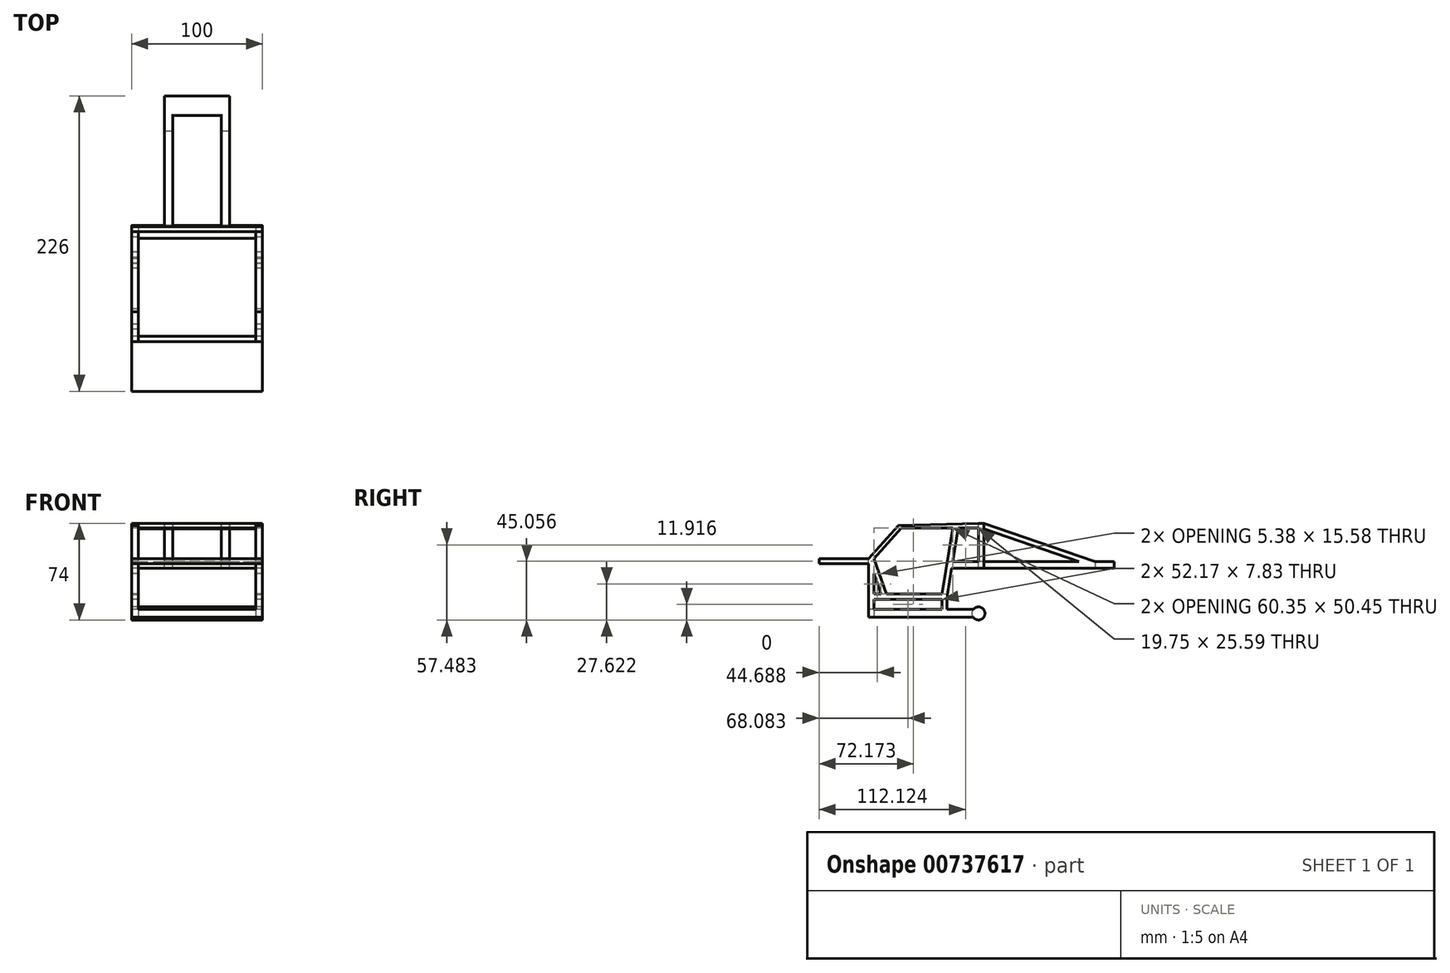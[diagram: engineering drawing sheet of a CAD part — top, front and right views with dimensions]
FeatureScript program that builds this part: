
annotation { "Feature Type Name" : "Feature", "Feature Type Description" : "" }
export const myFeature = defineFeature(function(context is Context, id is Id, definition is map)
    precondition{}
    {
        {
            var Q0;
            Q0=qCreatedBy(makeId("Right.planeOp"),FACE);
            var sketch = newSketch(context, id + "F0", { "sketchPlane" : qUnion([Q0])});
            skLineSegment(sketch, "E0.bottom", {"start": v(35, -26) * mm, "end": v(-45, -26) * mm});
            skLineSegment(sketch, "E0.top", {"start": v(35, -32) * mm, "end": v(-45, -32) * mm});
            skLineSegment(sketch, "E0.left", {"start": v(35, -26) * mm, "end": v(35, -32) * mm});
            skLineSegment(sketch, "E0.right", {"start": v(-45, -26) * mm, "end": v(-45, -32) * mm});
            skLineSegment(sketch, "E1.bottom", {"start": v(35, -32) * mm, "end": v(39, -32) * mm});
            skLineSegment(sketch, "E1.top", {"start": v(35, 40) * mm, "end": v(39, 40) * mm});
            skLineSegment(sketch, "E1.left", {"start": v(35, -32) * mm, "end": v(35, 40) * mm});
            skLineSegment(sketch, "E1.right", {"start": v(39, -32) * mm, "end": v(39, 40) * mm});
            skLineSegment(sketch, "E2", {"start": v(35, -26) * mm, "end": v(39, -26) * mm});
            skLineSegment(sketch, "E3.bottom", {"start": v(-45, -32) * mm, "end": v(-49, -32) * mm});
            skLineSegment(sketch, "E3.top", {"start": v(-45, 13) * mm, "end": v(-49, 13) * mm});
            skLineSegment(sketch, "E3.left", {"start": v(-45, -32) * mm, "end": v(-45, 13) * mm});
            skLineSegment(sketch, "E3.right", {"start": v(-49, -32) * mm, "end": v(-49, 13) * mm});
            skLineSegment(sketch, "E4", {"start": v(-45, -26) * mm, "end": v(-49, -26) * mm});
            skLineSegment(sketch, "E5", {"start": v(-49, 13) * mm, "end": v(-26.27, 38.28) * mm});
            skLineSegment(sketch, "E6", {"start": v(-26.27, 38.28) * mm, "end": v(-24.04, 36.28) * mm});
            skLineSegment(sketch, "E7", {"start": v(-24.04, 36.28) * mm, "end": v(-45, 13) * mm});
            skLineSegment(sketch, "E8", {"start": v(35, 40) * mm, "end": v(-26.27, 38.28) * mm});
            skLineSegment(sketch, "E9", {"start": v(-24.04, 36.28) * mm, "end": v(35, 36.28) * mm});
            skLineSegment(sketch, "E10", {"start": v(-45, 13) * mm, "end": v(-35.62, -14.17) * mm});
            skLineSegment(sketch, "E11", {"start": v(-35.62, -14.17) * mm, "end": v(7.17, -14.17) * mm});
            skLineSegment(sketch, "E12", {"start": v(7.17, -14.17) * mm, "end": v(15.86, 39.46) * mm});
            skLineSegment(sketch, "E13", {"start": v(7.17, -14.17) * mm, "end": v(11.11, -14.8) * mm});
            skLineSegment(sketch, "E14", {"start": v(11.11, -14.8) * mm, "end": v(19.91, 39.46) * mm});
            skLineSegment(sketch, "E15", {"start": v(-49, 13) * mm, "end": v(-39.62, -14.17) * mm});
            skLineSegment(sketch, "E16", {"start": v(-39.62, -14.17) * mm, "end": v(-35.62, -14.17) * mm});
            skLineSegment(sketch, "E17", {"start": v(-39.62, -14.17) * mm, "end": v(-39.62, -18.17) * mm});
            skLineSegment(sketch, "E18", {"start": v(-39.62, -18.17) * mm, "end": v(10.75, -18.17) * mm});
            skLineSegment(sketch, "E19", {"start": v(10.75, -18.17) * mm, "end": v(11.11, -14.8) * mm});
            skLineSegment(sketch, "E20", {"start": v(7.17, -14.17) * mm, "end": v(7.17, -18.17) * mm});
            skLineSegment(sketch, "E21", {"start": v(7.17, -18.17) * mm, "end": v(7.17, -26) * mm});
            skLineSegment(sketch, "E22", {"start": v(10.75, -18.17) * mm, "end": v(10.75, -26) * mm});
            skLineSegment(sketch, "E23", {"start": v(10.75, -26) * mm, "end": v(7.17, -26) * mm});
            skLineSegment(sketch, "E24.bottom", {"start": v(-39.62, -18.17) * mm, "end": v(-45, -18.17) * mm});
            skLineSegment(sketch, "E24.top", {"start": v(-39.62, -14.17) * mm, "end": v(-45, -14.17) * mm});
            skLineSegment(sketch, "E24.left", {"start": v(-39.62, -18.17) * mm, "end": v(-39.62, -14.17) * mm});
            skLineSegment(sketch, "E24.right", {"start": v(-45, -18.17) * mm, "end": v(-45, -14.17) * mm});
            skCircle(sketch, "E25", {"center": v(35, -29) * mm, "radius": 5 * mm});
            skLineSegment(sketch, "E26.bottom", {"start": v(39, 10.69) * mm, "end": v(111.81, 10.69) * mm});
            skLineSegment(sketch, "E26.top", {"start": v(39, 5.69) * mm, "end": v(139, 5.69) * mm});
            skLineSegment(sketch, "E26.left", {"start": v(39, 10.69) * mm, "end": v(39, 5.69) * mm});
            skLineSegment(sketch, "E26.right", {"start": v(139, 10.69) * mm, "end": v(139, 5.69) * mm});
            skLineSegment(sketch, "E27.bottom", {"start": v(39, 5.69) * mm, "end": v(14.44, 5.69) * mm});
            skLineSegment(sketch, "E27.top", {"start": v(39, 10.69) * mm, "end": v(15.25, 10.69) * mm});
            skLineSegment(sketch, "E27.left", {"start": v(39, 5.69) * mm, "end": v(39, 10.69) * mm});
            skPoint(sketch, "E27.right.end.orphan", {"position": v(11.2, 10.69) * mm});
            skLineSegment(sketch, "E28", {"start": v(39, 40) * mm, "end": v(124.1, 10.69) * mm});
            skLineSegment(sketch, "E29", {"start": v(111.81, 10.69) * mm, "end": v(39, 35.77) * mm});
            skPoint(sketch, "E29.endSnap0", {"position": v(37, 40) * mm});
            skLineSegment(sketch, "E30.trimOffspring", {"start": v(124.1, 10.69) * mm, "end": v(139, 10.69) * mm});
            skLineSegment(sketch, "E31", {"start": v(-49, 13) * mm, "end": v(-87, 13) * mm});
            skLineSegment(sketch, "E32", {"start": v(-87, 13) * mm, "end": v(-87, 9) * mm});
            skLineSegment(sketch, "E33", {"start": v(-87, 9) * mm, "end": v(-49, 9) * mm});
            skLineSegment(sketch, "E34", {"start": v(10.75, -26) * mm, "end": v(10.75, -32) * mm});
            skLineSegment(sketch, "E35", {"start": v(39, 35.77) * mm, "end": v(35, 36.28) * mm});
            skSolve(sketch);
        }
        {
            var Q0;
            {var subQ0=sQuery(id+"F0.wireOp",EDGE,"E4");Q0=makeQuery(id+"F0.imprint","IMPRINT",FACE,{"disambiguationData":[TD([[makeQuery(id+"F0.imprint","IMPRINT",EDGE,{"derivedFrom":subQ0}),-1.0]])]});}
            var Q1;
            Q1=makeQuery(id+"F0.imprint","IMPRINT",FACE,{"disambiguationData":[TD([[makeQuery(id+"F0.imprint","IMPRINT",EDGE,{"derivedFrom":sQuery(id+"F0.wireOp",EDGE,"E0.right")}),-1.0]])]});
            var Q2;
            Q2=makeQuery(id+"F0.imprint","IMPRINT",FACE,{"disambiguationData":[TD([[makeQuery(id+"F0.imprint","IMPRINT",EDGE,{"derivedFrom":sQuery(id+"F0.wireOp",EDGE,"E3.top")}),-1.0]])]});
            var Q3;
            {var subQ0=sQuery(id+"F0.wireOp",EDGE,"E6");Q3=makeQuery(id+"F0.imprint","IMPRINT",FACE,{"disambiguationData":[TD([[makeQuery(id+"F0.imprint","IMPRINT",EDGE,{"derivedFrom":subQ0}),1.0]])]});}
            var Q4;
            {var subQ0=sQuery(id+"F0.wireOp",EDGE,"E9");var subQ1=makeQuery(id+"F0.imprint","INTERSECT",VERTEX,{"derivedFrom":[subQ0,sQuery(id+"F0.wireOp",EDGE,"E14")]});Q4=makeQuery(id+"F0.imprint","IMPRINT",FACE,{"disambiguationData":[TD([[makeQuery(id+"F0.imprint","IMPRINT",EDGE,{"disambiguationData":[TD([[subQ1,1.0]])],"derivedFrom":subQ0}),1.0]])]});}
            var Q5;
            {var subQ0=sQuery(id+"F0.wireOp",EDGE,"E3.top");Q5=makeQuery(id+"F0.imprint","IMPRINT",FACE,{"disambiguationData":[TD([[makeQuery(id+"F0.imprint","IMPRINT",EDGE,{"derivedFrom":subQ0}),1.0]])]});}
            var Q6;
            {var subQ0=sQuery(id+"F0.wireOp",EDGE,"E10");Q6=makeQuery(id+"F0.imprint","IMPRINT",FACE,{"disambiguationData":[TD([[makeQuery(id+"F0.imprint","IMPRINT",EDGE,{"derivedFrom":subQ0}),-1.0]])]});}
            var Q7;
            Q7=makeQuery(id+"F0.imprint","IMPRINT",FACE,{"disambiguationData":[TD([[makeQuery(id+"F0.imprint","IMPRINT",EDGE,{"derivedFrom":sQuery(id+"F0.wireOp",EDGE,"E11")}),-1.0]])]});
            var Q8;
            Q8=makeQuery(id+"F0.imprint","IMPRINT",FACE,{"disambiguationData":[TD([[makeQuery(id+"F0.imprint","IMPRINT",EDGE,{"derivedFrom":sQuery(id+"F0.wireOp",EDGE,"E13")}),-1.0]])]});
            var Q9;
            {var subQ4=sQuery(id+"F0.wireOp",EDGE,"E13");Q9=makeQuery(id+"F0.imprint","IMPRINT",FACE,{"disambiguationData":[TD([[makeQuery(id+"F0.imprint","IMPRINT",EDGE,{"derivedFrom":subQ4}),1.0]])]});}
            var Q10;
            {var subQ4=sQuery(id+"F0.wireOp",EDGE,"E13");Q10=makeQuery(id+"F0.imprint","IMPRINT",FACE,{"disambiguationData":[TD([[makeQuery(id+"F0.imprint","IMPRINT",EDGE,{"derivedFrom":subQ4}),1.0]])]});}
            var Q11;
            Q11=makeQuery(id+"F0.imprint","IMPRINT",FACE,{"disambiguationData":[TD([[makeQuery(id+"F0.imprint","IMPRINT",EDGE,{"derivedFrom":sQuery(id+"F0.wireOp",EDGE,"E17")}),-1.0]])]});
            var Q12;
            {var subQ0=sQuery(id+"F0.wireOp",EDGE,"E21");Q12=makeQuery(id+"F0.imprint","IMPRINT",FACE,{"disambiguationData":[TD([[makeQuery(id+"F0.imprint","IMPRINT",EDGE,{"derivedFrom":subQ0}),1.0]])]});}
            var Q13;
            {var subQ2=sQuery(id+"F0.wireOp",EDGE,"E0.right");Q13=makeQuery(id+"F0.imprint","IMPRINT",FACE,{"disambiguationData":[TD([[makeQuery(id+"F0.imprint","IMPRINT",EDGE,{"derivedFrom":subQ2}),1.0]])]});}
            var Q14;
            {var subQ0=sQuery(id+"F0.wireOp",EDGE,"E1.left");var subQ3=sQuery(id+"F0.wireOp",EDGE,"E25");var subQ5=makeQuery(id+"F0.imprint","INTERSECT",VERTEX,{"derivedFrom":[subQ0,subQ3]});Q14=makeQuery(id+"F0.imprint","IMPRINT",FACE,{"disambiguationData":[TD([[makeQuery(id+"F0.imprint","IMPRINT",EDGE,{"disambiguationData":[TD([[subQ5,-1.0]])],"derivedFrom":subQ3}),1.0]])]});}
            var Q15;
            {var subQ0=sQuery(id+"F0.wireOp",EDGE,"E0.left");Q15=makeQuery(id+"F0.imprint","IMPRINT",FACE,{"disambiguationData":[TD([[makeQuery(id+"F0.imprint","IMPRINT",EDGE,{"derivedFrom":subQ0}),-1.0]])]});}
            var Q16;
            {var subQ3=sQuery(id+"F0.wireOp",EDGE,"E1.bottom");Q16=makeQuery(id+"F0.imprint","IMPRINT",FACE,{"disambiguationData":[TD([[makeQuery(id+"F0.imprint","IMPRINT",EDGE,{"derivedFrom":subQ3}),-1.0]])]});}
            var Q17;
            Q17=makeQuery(id+"F0.imprint","IMPRINT",FACE,{"disambiguationData":[TD([[makeQuery(id+"F0.imprint","IMPRINT",EDGE,{"derivedFrom":sQuery(id+"F0.wireOp",EDGE,"E0.left")}),1.0]])]});
            var Q18;
            {var subQ0=sQuery(id+"F0.wireOp",EDGE,"E2");Q18=makeQuery(id+"F0.imprint","IMPRINT",FACE,{"disambiguationData":[TD([[makeQuery(id+"F0.imprint","IMPRINT",EDGE,{"derivedFrom":subQ0}),1.0]])]});}
            var Q19;
            {var subQ0=sQuery(id+"F0.wireOp",EDGE,"E25");var subQ1=sQuery(id+"F0.wireOp",EDGE,"E1.right");var subQ2=makeQuery(id+"F0.imprint","INTERSECT",VERTEX,{"derivedFrom":[sQuery(id+"F0.wireOp",EDGE,"E1.bottom"),subQ1,subQ0]});Q19=makeQuery(id+"F0.imprint","IMPRINT",FACE,{"disambiguationData":[TD([[makeQuery(id+"F0.imprint","IMPRINT",EDGE,{"disambiguationData":[TD([[subQ2,-1.0]])],"derivedFrom":subQ1}),-1.0]])]});}
            var Q20;
            {var subQ0=sQuery(id+"F0.wireOp",EDGE,"E34");Q20=makeQuery(id+"F0.imprint","IMPRINT",FACE,{"disambiguationData":[TD([[makeQuery(id+"F0.imprint","IMPRINT",EDGE,{"derivedFrom":subQ0}),1.0]])]});}
            var Q21;
            {var subQ0=sQuery(id+"F0.wireOp",EDGE,"E27.bottom");var subQ1=sQuery(id+"F0.wireOp",EDGE,"E1.left");var subQ2=makeQuery(id+"F0.imprint","INTERSECT",VERTEX,{"derivedFrom":[subQ1,subQ0]});Q21=makeQuery(id+"F0.imprint","IMPRINT",FACE,{"disambiguationData":[TD([[makeQuery(id+"F0.imprint","IMPRINT",EDGE,{"disambiguationData":[TD([[subQ2,-1.0]])],"derivedFrom":subQ1}),1.0]])]});}
            var Q22;
            {var subQ0=sQuery(id+"F0.wireOp",EDGE,"E1.top");Q22=makeQuery(id+"F0.imprint","IMPRINT",FACE,{"disambiguationData":[TD([[makeQuery(id+"F0.imprint","IMPRINT",EDGE,{"derivedFrom":subQ0}),-1.0]])]});}
            var Q23;
            {var subQ0=sQuery(id+"F0.wireOp",EDGE,"E27.bottom");var subQ1=sQuery(id+"F0.wireOp",EDGE,"E1.left");var subQ2=makeQuery(id+"F0.imprint","INTERSECT",VERTEX,{"derivedFrom":[subQ1,subQ0]});Q23=makeQuery(id+"F0.imprint","IMPRINT",FACE,{"disambiguationData":[TD([[makeQuery(id+"F0.imprint","IMPRINT",EDGE,{"disambiguationData":[TD([[subQ2,-1.0]])],"derivedFrom":subQ1}),-1.0]])]});}
            var Q24;
            {var subQ0=sQuery(id+"F0.wireOp",EDGE,"E31");Q24=makeQuery(id+"F0.imprint","IMPRINT",FACE,{"disambiguationData":[TD([[makeQuery(id+"F0.imprint","IMPRINT",EDGE,{"derivedFrom":subQ0}),1.0]])]});}
            var Q25;
            {var subQ3=sQuery(id+"F0.wireOp",EDGE,"E35");Q25=makeQuery(id+"F0.imprint","IMPRINT",FACE,{"disambiguationData":[TD([[makeQuery(id+"F0.imprint","IMPRINT",EDGE,{"derivedFrom":subQ3}),1.0]])]});}
            extrude(context, id + "F1", {"entities" : qUnion([Q0, Q1, Q2, Q3, Q4, Q5, Q6, Q7, Q8, Q9, Q10, Q11, Q12, Q13, Q14, Q15, Q16, Q17, Q18, Q19, Q20, Q21, Q22, Q23, Q24, Q25]), "endBound" : BoundingType.SYMMETRIC, "depth" : 100 * mm, "offsetDistance" : 25 * mm});
        }
        {
            var Q0;
            {var subQ3=sQuery(id+"F0.wireOp",EDGE,"E35");Q0=makeQuery(id+"F0.imprint","IMPRINT",FACE,{"disambiguationData":[TD([[makeQuery(id+"F0.imprint","IMPRINT",EDGE,{"derivedFrom":subQ3}),1.0]])]});}
            extrude(context, id + "F2", {"entities" : qUnion([Q0]), "operationType" : NewBodyOperationType.REMOVE, "endBound" : BoundingType.SYMMETRIC, "oppositeDirection" : true, "depth" : 90 * mm, "offsetDistance" : 25 * mm});
        }
        {
            var Q0;
            {var subQ4=sQuery(id+"F0.wireOp",EDGE,"E13");Q0=makeQuery(id+"F0.imprint","IMPRINT",FACE,{"disambiguationData":[TD([[makeQuery(id+"F0.imprint","IMPRINT",EDGE,{"derivedFrom":subQ4}),1.0]])]});}
            var Q1;
            {var subQ0=sQuery(id+"F0.wireOp",EDGE,"E6");Q1=makeQuery(id+"F0.imprint","IMPRINT",FACE,{"disambiguationData":[TD([[makeQuery(id+"F0.imprint","IMPRINT",EDGE,{"derivedFrom":subQ0}),1.0]])]});}
            var Q2;
            {var subQ0=sQuery(id+"F0.wireOp",EDGE,"E9");var subQ1=makeQuery(id+"F0.imprint","INTERSECT",VERTEX,{"derivedFrom":[subQ0,sQuery(id+"F0.wireOp",EDGE,"E14")]});Q2=makeQuery(id+"F0.imprint","IMPRINT",FACE,{"disambiguationData":[TD([[makeQuery(id+"F0.imprint","IMPRINT",EDGE,{"disambiguationData":[TD([[subQ1,1.0]])],"derivedFrom":subQ0}),1.0]])]});}
            var Q3;
            Q3=makeQuery(id+"F0.imprint","IMPRINT",FACE,{"disambiguationData":[TD([[makeQuery(id+"F0.imprint","IMPRINT",EDGE,{"derivedFrom":sQuery(id+"F0.wireOp",EDGE,"E3.top")}),-1.0]])]});
            var Q4;
            {var subQ0=sQuery(id+"F0.wireOp",EDGE,"E3.top");Q4=makeQuery(id+"F0.imprint","IMPRINT",FACE,{"disambiguationData":[TD([[makeQuery(id+"F0.imprint","IMPRINT",EDGE,{"derivedFrom":subQ0}),1.0]])]});}
            var Q5;
            {var subQ0=sQuery(id+"F0.wireOp",EDGE,"E10");Q5=makeQuery(id+"F0.imprint","IMPRINT",FACE,{"disambiguationData":[TD([[makeQuery(id+"F0.imprint","IMPRINT",EDGE,{"derivedFrom":subQ0}),-1.0]])]});}
            var Q6;
            Q6=makeQuery(id+"F0.imprint","IMPRINT",FACE,{"disambiguationData":[TD([[makeQuery(id+"F0.imprint","IMPRINT",EDGE,{"derivedFrom":sQuery(id+"F0.wireOp",EDGE,"E11")}),-1.0]])]});
            var Q7;
            Q7=makeQuery(id+"F0.imprint","IMPRINT",FACE,{"disambiguationData":[TD([[makeQuery(id+"F0.imprint","IMPRINT",EDGE,{"derivedFrom":sQuery(id+"F0.wireOp",EDGE,"E13")}),-1.0]])]});
            var Q8;
            Q8=makeQuery(id+"F0.imprint","IMPRINT",FACE,{"disambiguationData":[TD([[makeQuery(id+"F0.imprint","IMPRINT",EDGE,{"derivedFrom":sQuery(id+"F0.wireOp",EDGE,"E17")}),-1.0]])]});
            var Q9;
            {var subQ0=sQuery(id+"F0.wireOp",EDGE,"E21");Q9=makeQuery(id+"F0.imprint","IMPRINT",FACE,{"disambiguationData":[TD([[makeQuery(id+"F0.imprint","IMPRINT",EDGE,{"derivedFrom":subQ0}),1.0]])]});}
            var Q10;
            {var subQ2=sQuery(id+"F0.wireOp",EDGE,"E0.right");Q10=makeQuery(id+"F0.imprint","IMPRINT",FACE,{"disambiguationData":[TD([[makeQuery(id+"F0.imprint","IMPRINT",EDGE,{"derivedFrom":subQ2}),1.0]])]});}
            var Q11;
            {var subQ0=sQuery(id+"F0.wireOp",EDGE,"E34");Q11=makeQuery(id+"F0.imprint","IMPRINT",FACE,{"disambiguationData":[TD([[makeQuery(id+"F0.imprint","IMPRINT",EDGE,{"derivedFrom":subQ0}),1.0]])]});}
            var Q12;
            {var subQ0=sQuery(id+"F0.wireOp",EDGE,"E27.bottom");var subQ1=sQuery(id+"F0.wireOp",EDGE,"E1.left");var subQ2=makeQuery(id+"F0.imprint","INTERSECT",VERTEX,{"derivedFrom":[subQ1,subQ0]});Q12=makeQuery(id+"F0.imprint","IMPRINT",FACE,{"disambiguationData":[TD([[makeQuery(id+"F0.imprint","IMPRINT",EDGE,{"disambiguationData":[TD([[subQ2,-1.0]])],"derivedFrom":subQ1}),1.0]])]});}
            extrude(context, id + "F3", {"entities" : qUnion([Q0, Q1, Q2, Q3, Q4, Q5, Q6, Q7, Q8, Q9, Q10, Q11, Q12]), "operationType" : NewBodyOperationType.REMOVE, "endBound" : BoundingType.SYMMETRIC, "oppositeDirection" : true, "depth" : 90 * mm, "offsetDistance" : 25 * mm});
        }
        {
            var Q0;
            {var subQ0=sQuery(id+"F0.wireOp",EDGE,"E4");Q0=makeQuery(id+"F0.imprint","IMPRINT",FACE,{"disambiguationData":[TD([[makeQuery(id+"F0.imprint","IMPRINT",EDGE,{"derivedFrom":subQ0}),-1.0]])]});}
            extrude(context, id + "F4", {"entities" : qUnion([Q0]), "operationType" : NewBodyOperationType.REMOVE, "endBound" : BoundingType.SYMMETRIC, "oppositeDirection" : true, "depth" : 90 * mm, "offsetDistance" : 25 * mm});
        }
        {
            var Q0;
            {var subQ1=sQuery(id+"F0.wireOp",EDGE,"E26.bottom");Q0=makeQuery(id+"F0.imprint","IMPRINT",FACE,{"disambiguationData":[TD([[makeQuery(id+"F0.imprint","IMPRINT",EDGE,{"derivedFrom":subQ1}),-1.0]])]});}
            extrude(context, id + "F5", {"entities" : qUnion([Q0]), "operationType" : NewBodyOperationType.ADD, "endBound" : BoundingType.SYMMETRIC, "depth" : 50 * mm, "offsetDistance" : 25 * mm});
        }
        {
            var Q0;
            {var subQ1=sQuery(id+"F0.wireOp",EDGE,"E26.bottom");Q0=makeQuery(id+"F0.imprint","IMPRINT",FACE,{"disambiguationData":[TD([[makeQuery(id+"F0.imprint","IMPRINT",EDGE,{"derivedFrom":subQ1}),-1.0]])]});}
            extrude(context, id + "F6", {"entities" : qUnion([Q0]), "operationType" : NewBodyOperationType.REMOVE, "endBound" : BoundingType.SYMMETRIC, "oppositeDirection" : true, "depth" : 37 * mm, "offsetDistance" : 25 * mm});
        }
        {
            var Q0;
            Q0=makeQuery(id+"F6.boolean.opBoolean","COPY",FACE,{"derivedFrom":makeQuery(id+"F6.opExtrude","CAP_FACE",FACE,{"disambiguationData":[OSD([sQuery(id+"F0.wireOp",EDGE,"E1.right"),sQuery(id+"F0.wireOp",EDGE,"E26.bottom"),sQuery(id+"F0.wireOp",EDGE,"E26.top"),sQuery(id+"F0.wireOp",EDGE,"E26.right"),sQuery(id+"F0.wireOp",EDGE,"E28"),sQuery(id+"F0.wireOp",EDGE,"E29"),sQuery(id+"F0.wireOp",EDGE,"E30.trimOffspring")])],"isStart":false})});
            var sketch = newSketch(context, id + "F7", { "sketchPlane" : qUnion([Q0])});
            skLineSegment(sketch, "E36.bottom", {"start": v(124.1, 10.69) * mm, "end": v(139, 10.69) * mm});
            skLineSegment(sketch, "E36.top", {"start": v(124.1, 5.69) * mm, "end": v(139, 5.69) * mm});
            skLineSegment(sketch, "E36.left", {"start": v(124.1, 10.69) * mm, "end": v(124.1, 5.69) * mm});
            skLineSegment(sketch, "E36.right", {"start": v(139, 10.69) * mm, "end": v(139, 5.69) * mm});
            skSolve(sketch);
        }
        {
            var Q0;
            Q0=makeQuery(id+"F7.imprint","IMPRINT",FACE,{"disambiguationData":[TD([[makeQuery(id+"F7.imprint","IMPRINT",EDGE,{"derivedFrom":sQuery(id+"F7.wireOp",EDGE,"E36.bottom")}),-1.0]])]});
            extrude(context, id + "F8", {"entities" : qUnion([Q0]), "operationType" : NewBodyOperationType.ADD, "endBound" : BoundingType.UP_TO_NEXT, "depth" : 25 * mm, "offsetDistance" : 25 * mm});
        }
        {
            var Q0;
            {var subQ0=sQuery(id+"F0.wireOp",EDGE,"E30.trimOffspring");var subQ1=sQuery(id+"F0.wireOp",EDGE,"E29");var subQ2=sQuery(id+"F0.wireOp",EDGE,"E28");var subQ3=sQuery(id+"F0.wireOp",EDGE,"E26.right");var subQ4=sQuery(id+"F0.wireOp",EDGE,"E26.top");var subQ5=sQuery(id+"F0.wireOp",EDGE,"E26.bottom");var subQ6=sQuery(id+"F0.wireOp",EDGE,"E1.right");Q0=makeQuery(id+"F6.boolean.opBoolean","SPLIT",EDGE,{"disambiguationData":[TD([makeQuery(id+"F5.opExtrude","CAP_FACE",FACE,{"disambiguationData":[OSD([subQ6,subQ5,subQ4,subQ3,subQ2,subQ1,subQ0])],"isStart":true})])],"derivedFrom":makeQuery(id+"F5.opExtrude","SWEPT_EDGE",EDGE,{"disambiguationData":[OSD([subQ2,subQ0])]})});}
            var Q1;
            {var subQ0=sQuery(id+"F0.wireOp",EDGE,"E30.trimOffspring");var subQ1=sQuery(id+"F0.wireOp",EDGE,"E29");var subQ2=sQuery(id+"F0.wireOp",EDGE,"E28");var subQ3=sQuery(id+"F0.wireOp",EDGE,"E26.right");var subQ4=sQuery(id+"F0.wireOp",EDGE,"E26.top");var subQ5=sQuery(id+"F0.wireOp",EDGE,"E26.bottom");var subQ6=sQuery(id+"F0.wireOp",EDGE,"E1.right");Q1=makeQuery(id+"F6.boolean.opBoolean","SPLIT",EDGE,{"disambiguationData":[TD([makeQuery(id+"F5.opExtrude","CAP_FACE",FACE,{"disambiguationData":[OSD([subQ6,subQ5,subQ4,subQ3,subQ2,subQ1,subQ0])],"isStart":false})])],"derivedFrom":makeQuery(id+"F5.opExtrude","SWEPT_EDGE",EDGE,{"disambiguationData":[OSD([subQ2,subQ0])]})});}
            fillet(context, id + "F9", {"entities" : qUnion([Q0, Q1]), "radius" : 5 * mm, "tangentPropagation" : true, "allowEdgeOverflow" : false});
        }
    });
